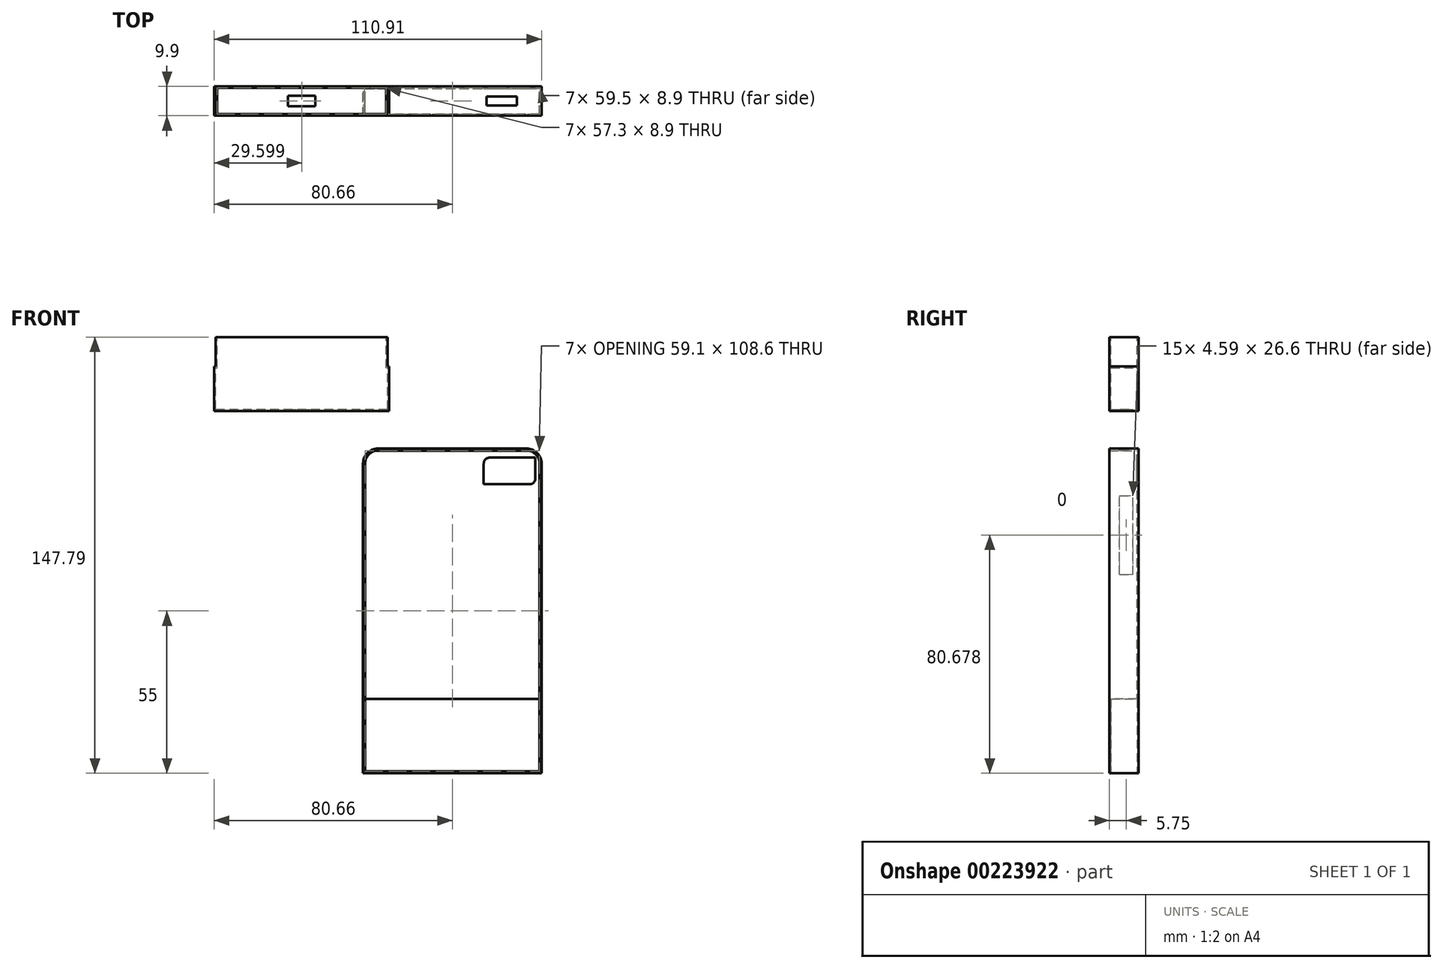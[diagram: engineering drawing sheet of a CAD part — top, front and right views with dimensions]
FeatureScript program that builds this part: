
annotation { "Feature Type Name" : "Feature", "Feature Type Description" : "" }
export const myFeature = defineFeature(function(context is Context, id is Id, definition is map)
    precondition{}
    {
        {
            var Q0;
            Q0=qCreatedBy(makeId("Front.planeOp"),FACE);
            var sketch = newSketch(context, id + "F0", { "sketchPlane" : qUnion([Q0])});
            skLineSegment(sketch, "E0", {"start": v(5, 0) * mm, "end": v(55.5, 0) * mm});
            skLineSegment(sketch, "E1", {"start": v(60.5, -5) * mm, "end": v(60.5, -110) * mm});
            skLineSegment(sketch, "E2", {"start": v(0, -5) * mm, "end": v(0, -110) * mm});
            skLineSegment(sketch, "E3", {"start": v(0, -110) * mm, "end": v(60.5, -110) * mm});
            skPoint(sketch, "E4.visualSharp", {"position": v(0, 0) * mm});
            skArc(sketch, "E4.filletArc", {"start": v(5, 0) * mm, "mid": v(1.46, -1.46) * mm, "end": v(0, -5) * mm});
            skPoint(sketch, "E5.visualSharp", {"position": v(60.5, 0) * mm});
            skArc(sketch, "E5.filletArc", {"start": v(60.5, -5) * mm, "mid": v(59.04, -1.46) * mm, "end": v(55.5, 0) * mm});
            skSolve(sketch);
        }
        {
            var Q0;
            Q0=qCreatedBy(makeId("Front.planeOp"),FACE);
            var sketch = newSketch(context, id + "F1", { "sketchPlane" : qUnion([Q0])});
            skLineSegment(sketch, "E6.bottom", {"start": v(58.4, -3.07) * mm, "end": v(42.9, -3.07) * mm});
            skLineSegment(sketch, "E6.top", {"start": v(56.4, -12.07) * mm, "end": v(40.9, -12.07) * mm});
            skLineSegment(sketch, "E6.left", {"start": v(58.4, -3.07) * mm, "end": v(58.4, -10.07) * mm});
            skLineSegment(sketch, "E6.right", {"start": v(40.9, -5.07) * mm, "end": v(40.9, -12.07) * mm});
            skArc(sketch, "E7.filletArc", {"start": v(42.9, -3.07) * mm, "mid": v(41.5, -3.65) * mm, "end": v(40.9, -5.07) * mm});
            skArc(sketch, "E8.filletArc", {"start": v(56.4, -12.07) * mm, "mid": v(57.82, -11.48) * mm, "end": v(58.4, -10.07) * mm});
            skSolve(sketch);
        }
        {
            var Q0;
            Q0 = qSketchRegion(id + "F0", true);
            extrude(context, id + "F2", {"entities" : qUnion([Q0]), "depth" : 9.9 * mm});
        }
        {
            var Q0;
            Q0=makeQuery(id+"F2.opExtrude","CAP_FACE",FACE,{"disambiguationData":[OSD([sQuery(id+"F0.wireOp",EDGE,"E0"),sQuery(id+"F0.wireOp",EDGE,"E1"),sQuery(id+"F0.wireOp",EDGE,"E2"),sQuery(id+"F0.wireOp",EDGE,"E3"),sQuery(id+"F0.wireOp",EDGE,"E4.filletArc"),sQuery(id+"F0.wireOp",EDGE,"E5.filletArc")])],"isStart":false});
            shell(context, id + "F3", {"entities" : qUnion([Q0]), "thickness" : 0.7 * mm});
        }
        {
            var Q0;
            Q0=makeQuery(id+"F2.opExtrude","SWEPT_FACE",FACE,{"disambiguationData":[OSD([sQuery(id+"F0.wireOp",EDGE,"E3")])]});
            var Q1;
            Q1=makeQuery(id+"F2.opExtrude","SWEPT_BODY",BODY,{"disambiguationData":[OSD([sQuery(id+"F0.wireOp",EDGE,"E0"),sQuery(id+"F0.wireOp",EDGE,"E1"),sQuery(id+"F0.wireOp",EDGE,"E2"),sQuery(id+"F0.wireOp",EDGE,"E3"),sQuery(id+"F0.wireOp",EDGE,"E4.filletArc"),sQuery(id+"F0.wireOp",EDGE,"E5.filletArc")])]});
            shell(context, id + "F4", {"entities" : qUnion([Q0]), "parts" : qUnion([Q1]), "thickness" : .5 * mm});
        }
        {
            var Q0;
            Q0=makeQuery(id+"F1.imprint","IMPRINT",FACE,{"disambiguationData":[TD([[makeQuery(id+"F1.imprint","IMPRINT",EDGE,{"derivedFrom":sQuery(id+"F1.wireOp",EDGE,"E6.bottom")}),1.0]])]});
            extrude(context, id + "F5", {"entities" : qUnion([Q0]), "operationType" : NewBodyOperationType.REMOVE, "depth" : 25 * mm});
        }
        {
            var Q0;
            Q0=makeQuery(id+"F2.opExtrude","SWEPT_FACE",FACE,{"disambiguationData":[OSD([sQuery(id+"F0.wireOp",EDGE,"E2")])]});
            var sketch = newSketch(context, id + "F6", { "sketchPlane" : qUnion([Q0])});
            skLineSegment(sketch, "E9", {"start": v(1.86, -16.02) * mm, "end": v(6.44, -16.02) * mm});
            skLineSegment(sketch, "E10", {"start": v(1.86, -16.02) * mm, "end": v(1.86, -42.62) * mm});
            skLineSegment(sketch, "E11", {"start": v(6.44, -16.02) * mm, "end": v(6.44, -42.62) * mm});
            skLineSegment(sketch, "E12", {"start": v(1.86, -42.62) * mm, "end": v(6.44, -42.62) * mm});
            skSolve(sketch);
        }
        {
            var Q0;
            Q0 = qSketchRegion(id + "F6", true);
            extrude(context, id + "F7", {"entities" : qUnion([Q0]), "operationType" : NewBodyOperationType.REMOVE, "oppositeDirection" : true, "depth" : 25 * mm});
        }
        {
            var Q0;
            Q0=makeQuery(id+"F4.opShell","OFFSET_FACE",FACE,{"disambiguationData":[OSD([sQuery(id+"F0.wireOp",EDGE,"E3")])]});
            var sketch = newSketch(context, id + "F8", { "sketchPlane" : qUnion([Q0])});
            skLineSegment(sketch, "E13", {"start": v(0.5, 9.4) * mm, "end": v(60, 9.4) * mm});
            skLineSegment(sketch, "E14", {"start": v(60, 9.4) * mm, "end": v(60, 0.5) * mm});
            skLineSegment(sketch, "E15", {"start": v(60, 0.5) * mm, "end": v(0.5, 0.5) * mm});
            skLineSegment(sketch, "E16", {"start": v(0.5, 0.5) * mm, "end": v(0.5, 9.4) * mm});
            skSolve(sketch);
        }
        {
            var Q0;
            Q0 = qSketchRegion(id + "F8", true);
            extrude(context, id + "F9", {"entities" : qUnion([Q0]), "operationType" : NewBodyOperationType.REMOVE, "oppositeDirection" : true, "depth" : 25 * mm});
        }
        {
            var Q0;
            Q0=makeQuery(id+"F2.opExtrude","SWEPT_FACE",FACE,{"disambiguationData":[OSD([sQuery(id+"F0.wireOp",EDGE,"E0")])]});
            var sketch = newSketch(context, id + "F10", { "sketchPlane" : qUnion([Q0])});
            skLineSegment(sketch, "E17", {"start": v(60.5, -4.95) * mm, "end": v(52.1, -4.95) * mm});
            skLineSegment(sketch, "E18", {"start": v(52.1, -4.95) * mm, "end": v(52.1, -6.45) * mm});
            skLineSegment(sketch, "E19", {"start": v(52.1, -4.95) * mm, "end": v(52.1, -3.45) * mm});
            skLineSegment(sketch, "E20", {"start": v(52.1, -3.45) * mm, "end": v(41.9, -3.45) * mm});
            skLineSegment(sketch, "E21", {"start": v(41.9, -3.45) * mm, "end": v(41.9, -6.45) * mm});
            skLineSegment(sketch, "E22", {"start": v(41.9, -6.45) * mm, "end": v(52.1, -6.45) * mm});
            skSolve(sketch);
        }
        {
            var Q0;
            Q0 = qSketchRegion(id + "F10", true);
            extrude(context, id + "F11", {"entities" : qUnion([Q0]), "operationType" : NewBodyOperationType.REMOVE, "oppositeDirection" : true, "depth" : 25 * mm});
        }
        {
            var Q0;
            Q0=qCreatedBy(makeId("Front.planeOp"),FACE);
            var sketch = newSketch(context, id + "F12", { "sketchPlane" : qUnion([Q0])});
            skLineSegment(sketch, "E23", {"start": v(8.79, 12.79) * mm, "end": v(-50.41, 12.79) * mm});
            skLineSegment(sketch, "E24", {"start": v(8.79, 12.79) * mm, "end": v(8.79, 27.79) * mm});
            skLineSegment(sketch, "E25", {"start": v(-50.41, 12.79) * mm, "end": v(-50.41, 27.79) * mm});
            skLineSegment(sketch, "E26", {"start": v(-50.41, 27.79) * mm, "end": v(-49.96, 27.79) * mm});
            skLineSegment(sketch, "E27", {"start": v(-49.96, 27.79) * mm, "end": v(-49.96, 37.79) * mm});
            skLineSegment(sketch, "E28", {"start": v(8.79, 27.79) * mm, "end": v(8.34, 27.79) * mm});
            skLineSegment(sketch, "E29", {"start": v(8.34, 27.79) * mm, "end": v(8.34, 37.79) * mm});
            skLineSegment(sketch, "E30", {"start": v(8.34, 37.79) * mm, "end": v(-49.96, 37.79) * mm});
            skLineSegment(sketch, "E31", {"start": v(-49.96, 27.79) * mm, "end": v(8.34, 27.79) * mm});
            skSolve(sketch);
        }
        {
            var Q0;
            Q0 = qSketchRegion(id + "F12", true);
            extrude(context, id + "F13", {"entities" : qUnion([Q0]), "depth" : 9.9 * mm});
        }
        {
            var Q0;
            Q0=makeQuery(id+"F13.opExtrude","SWEPT_FACE",FACE,{"disambiguationData":[OSD([sQuery(id+"F12.wireOp",EDGE,"E30")])]});
            shell(context, id + "F14", {"entities" : qUnion([Q0]), "thickness" : .5 * mm});
        }
        {
            var Q0;
            Q0=makeQuery(id+"F13.opExtrude","SWEPT_FACE",FACE,{"disambiguationData":[OSD([sQuery(id+"F12.wireOp",EDGE,"E23")])]});
            var sketch = newSketch(context, id + "F15", { "sketchPlane" : qUnion([Q0])});
            skLineSegment(sketch, "E32", {"start": v(-25.51, 5) * mm, "end": v(-25.51, 6.7) * mm});
            skLineSegment(sketch, "E33", {"start": v(-25.51, 5) * mm, "end": v(-25.51, 3.2) * mm});
            skLineSegment(sketch, "E34", {"start": v(-25.51, 3.2) * mm, "end": v(-16.21, 3.2) * mm});
            skLineSegment(sketch, "E35", {"start": v(-16.21, 4.9) * mm, "end": v(-16.21, 3.2) * mm});
            skLineSegment(sketch, "E36", {"start": v(-25.51, 6.7) * mm, "end": v(-16.21, 6.7) * mm});
            skLineSegment(sketch, "E37", {"start": v(-16.21, 6.7) * mm, "end": v(-16.21, 4.9) * mm});
            skSolve(sketch);
        }
        {
            var Q0;
            Q0 = qSketchRegion(id + "F15", true);
            extrude(context, id + "F16", {"entities" : qUnion([Q0]), "operationType" : NewBodyOperationType.REMOVE, "oppositeDirection" : true, "depth" : 25 * mm});
        }
    });
